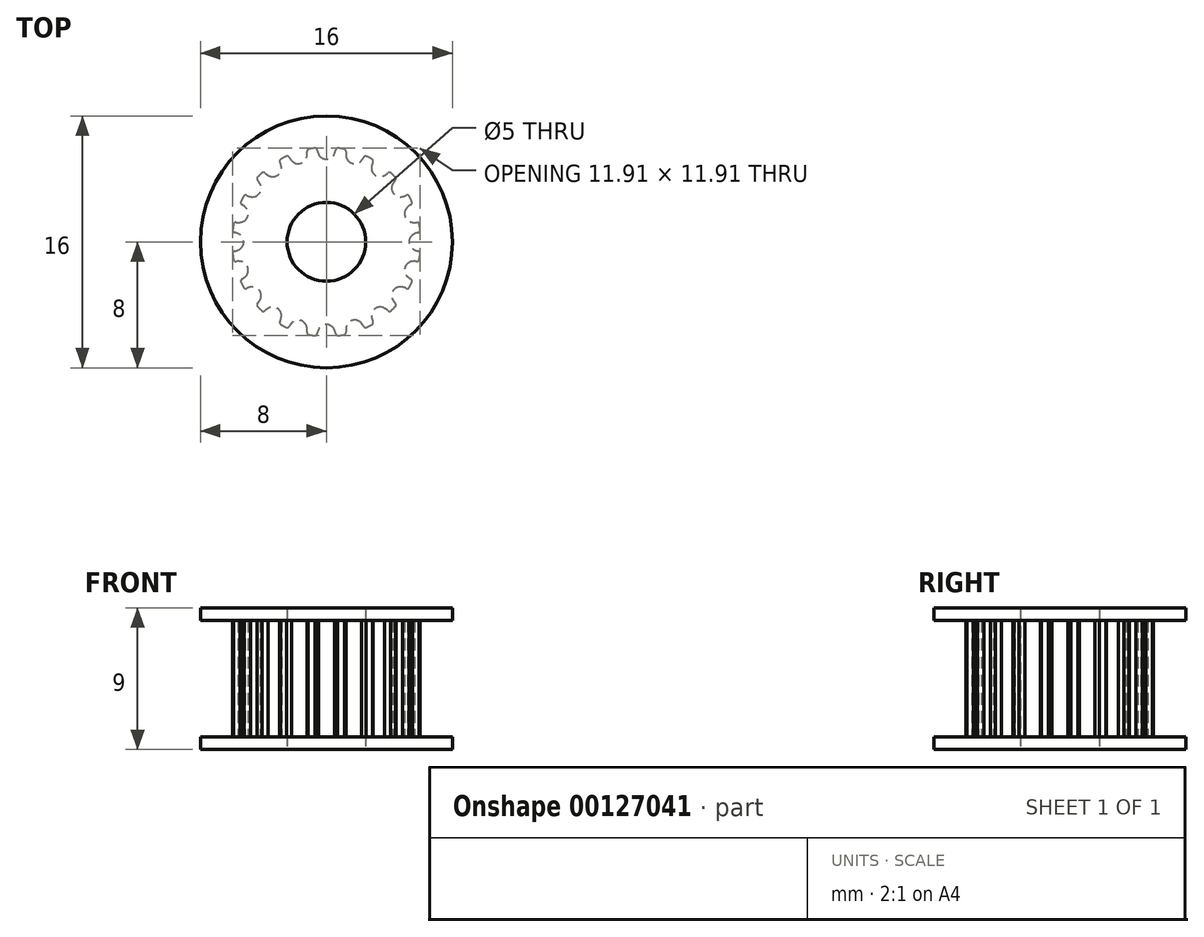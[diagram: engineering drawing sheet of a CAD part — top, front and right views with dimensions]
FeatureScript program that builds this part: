
annotation { "Feature Type Name" : "Feature", "Feature Type Description" : "" }
export const myFeature = defineFeature(function(context is Context, id is Id, definition is map)
    precondition{}
    {
        {
            var Q0;
            Q0=qCreatedBy(makeId("Top.planeOp"),FACE);
            var sketch = newSketch(context, id + "F0", { "sketchPlane" : qUnion([Q0])});
            skLineSegment(sketch, "E0", {"start": v(-19.17, 17.78) * mm, "end": v(-18.17, 17.78) * mm});
            skLineSegment(sketch, "E1", {"start": v(-18.17, 17.78) * mm, "end": v(-18.17, 18.4) * mm});
            skArc(sketch, "E2", {"start": v(-18.67, 18.85) * mm, "mid": v(-18.88, 19.07) * mm, "end": v(-19.17, 19.16) * mm});
            skArc(sketch, "E3", {"start": v(-18.58, 18.54) * mm, "mid": v(-18.61, 18.7) * mm, "end": v(-18.67, 18.85) * mm});
            skArc(sketch, "E4", {"start": v(-18.58, 18.54) * mm, "mid": v(-18.53, 18.44) * mm, "end": v(-18.43, 18.4) * mm});
            skLineSegment(sketch, "E5", {"start": v(-18.43, 18.4) * mm, "end": v(-18.17, 18.4) * mm});
            skArc(sketch, "E6.0.MirrorCS", {"start": v(-19.67, 18.85) * mm, "mid": v(-19.47, 19.07) * mm, "end": v(-19.17, 19.16) * mm});
            skArc(sketch, "E7.0.MirrorCS", {"start": v(-19.76, 18.54) * mm, "mid": v(-19.73, 18.7) * mm, "end": v(-19.67, 18.85) * mm});
            skArc(sketch, "E8.0.MirrorCS", {"start": v(-19.76, 18.54) * mm, "mid": v(-19.81, 18.44) * mm, "end": v(-19.91, 18.4) * mm});
            skLineSegment(sketch, "E9.0.MirrorCS", {"start": v(-19.91, 18.4) * mm, "end": v(-20.17, 18.4) * mm});
            skLineSegment(sketch, "E10.0.MirrorCS", {"start": v(-20.17, 17.78) * mm, "end": v(-20.17, 18.4) * mm});
            skLineSegment(sketch, "E11.0.MirrorCS", {"start": v(-19.17, 17.78) * mm, "end": v(-20.17, 17.78) * mm});
            skLineSegment(sketch, "E12.direction1", {"start": v(-20.17, 17.78) * mm, "end": v(-18.17, 17.78) * mm, "construction": true});
            skLineSegment(sketch, "E13", {"start": v(-20.17, 18.15) * mm, "end": v(-18.17, 18.15) * mm, "construction": true});
            skPoint(sketch, "E14", {"position": v(0, -5.25) * mm});
            skArc(sketch, "E15", {"start": v(0.51, -5.6) * mm, "mid": v(0, -5.25) * mm, "end": v(-0.51, -5.6) * mm});
            skArc(sketch, "E16", {"start": v(-0.51, -5.6) * mm, "mid": v(-0.56, -5.71) * mm, "end": v(-0.59, -5.83) * mm});
            skArc(sketch, "E17", {"start": v(0.59, -5.83) * mm, "mid": v(0.56, -5.71) * mm, "end": v(0.51, -5.6) * mm});
            skArc(sketch, "E18", {"start": v(0.72, -5.96) * mm, "mid": v(0.94, -5.93) * mm, "end": v(1.16, -5.89) * mm});
            skArc(sketch, "E19", {"start": v(0.59, -5.83) * mm, "mid": v(0.66, -5.94) * mm, "end": v(0.8, -5.95) * mm});
            skArc(sketch, "E20", {"start": v(-0.59, -5.83) * mm, "mid": v(-0.66, -5.94) * mm, "end": v(-0.8, -5.95) * mm});
            skArc(sketch, "E21.1.0", {"start": v(2.22, -5.16) * mm, "mid": v(1.62, -5) * mm, "end": v(1.24, -5.48) * mm});
            skPoint(sketch, "E21.1.1", {"position": v(1.62, -5) * mm});
            skArc(sketch, "E21.1.2", {"start": v(1.24, -5.48) * mm, "mid": v(1.23, -5.6) * mm, "end": v(1.24, -5.73) * mm});
            skArc(sketch, "E21.1.3", {"start": v(2.36, -5.37) * mm, "mid": v(2.47, -5.44) * mm, "end": v(2.6, -5.41) * mm});
            skArc(sketch, "E21.1.4", {"start": v(1.24, -5.73) * mm, "mid": v(1.2, -5.85) * mm, "end": v(1.08, -5.9) * mm});
            skArc(sketch, "E21.1.5", {"start": v(2.36, -5.37) * mm, "mid": v(2.3, -5.26) * mm, "end": v(2.22, -5.16) * mm});
            skArc(sketch, "E22.3.2.0", {"start": v(3.7, -4.22) * mm, "mid": v(3.09, -4.25) * mm, "end": v(2.87, -4.83) * mm});
            skPoint(sketch, "E22.4.2.0", {"position": v(3.09, -4.25) * mm});
            skArc(sketch, "E22.5.2.0", {"start": v(2.87, -4.83) * mm, "mid": v(2.9, -4.95) * mm, "end": v(2.95, -5.07) * mm});
            skArc(sketch, "E22.9.2.0", {"start": v(3.9, -4.37) * mm, "mid": v(4.03, -4.41) * mm, "end": v(4.14, -4.35) * mm});
            skArc(sketch, "E22.13.2.0", {"start": v(2.95, -5.07) * mm, "mid": v(2.95, -5.2) * mm, "end": v(2.85, -5.28) * mm});
            skArc(sketch, "E22.17.2.0", {"start": v(3.9, -4.37) * mm, "mid": v(3.81, -4.3) * mm, "end": v(3.7, -4.22) * mm});
            skArc(sketch, "E22.3.3.0", {"start": v(4.83, -2.87) * mm, "mid": v(4.25, -3.09) * mm, "end": v(4.22, -3.7) * mm});
            skPoint(sketch, "E22.4.3.0", {"position": v(4.25, -3.09) * mm});
            skArc(sketch, "E22.5.3.0", {"start": v(4.22, -3.7) * mm, "mid": v(4.3, -3.81) * mm, "end": v(4.37, -3.9) * mm});
            skArc(sketch, "E22.9.3.0", {"start": v(5.07, -2.95) * mm, "mid": v(5.2, -2.95) * mm, "end": v(5.28, -2.85) * mm});
            skArc(sketch, "E22.13.3.0", {"start": v(4.37, -3.9) * mm, "mid": v(4.41, -4.03) * mm, "end": v(4.35, -4.14) * mm});
            skArc(sketch, "E22.17.3.0", {"start": v(5.07, -2.95) * mm, "mid": v(4.95, -2.9) * mm, "end": v(4.83, -2.87) * mm});
            skArc(sketch, "E22.3.4.0", {"start": v(5.48, -1.24) * mm, "mid": v(5, -1.62) * mm, "end": v(5.16, -2.22) * mm});
            skPoint(sketch, "E22.4.4.0", {"position": v(5, -1.62) * mm});
            skArc(sketch, "E22.5.4.0", {"start": v(5.16, -2.22) * mm, "mid": v(5.26, -2.3) * mm, "end": v(5.37, -2.36) * mm});
            skArc(sketch, "E22.9.4.0", {"start": v(5.73, -1.24) * mm, "mid": v(5.85, -1.2) * mm, "end": v(5.9, -1.08) * mm});
            skArc(sketch, "E22.13.4.0", {"start": v(5.37, -2.36) * mm, "mid": v(5.44, -2.47) * mm, "end": v(5.41, -2.6) * mm});
            skArc(sketch, "E22.17.4.0", {"start": v(5.73, -1.24) * mm, "mid": v(5.6, -1.23) * mm, "end": v(5.48, -1.24) * mm});
            skArc(sketch, "E22.3.5.0", {"start": v(5.6, 0.51) * mm, "mid": v(5.25, 0) * mm, "end": v(5.6, -0.51) * mm});
            skPoint(sketch, "E22.4.5.0", {"position": v(5.25, 0) * mm});
            skArc(sketch, "E22.5.5.0", {"start": v(5.6, -0.51) * mm, "mid": v(5.71, -0.56) * mm, "end": v(5.83, -0.59) * mm});
            skArc(sketch, "E22.9.5.0", {"start": v(5.83, 0.59) * mm, "mid": v(5.94, 0.66) * mm, "end": v(5.95, 0.8) * mm});
            skArc(sketch, "E22.13.5.0", {"start": v(5.83, -0.59) * mm, "mid": v(5.94, -0.66) * mm, "end": v(5.95, -0.8) * mm});
            skArc(sketch, "E22.17.5.0", {"start": v(5.83, 0.59) * mm, "mid": v(5.71, 0.56) * mm, "end": v(5.6, 0.51) * mm});
            skArc(sketch, "E22.3.6.0", {"start": v(5.16, 2.22) * mm, "mid": v(5, 1.62) * mm, "end": v(5.48, 1.24) * mm});
            skPoint(sketch, "E22.4.6.0", {"position": v(5, 1.62) * mm});
            skArc(sketch, "E22.5.6.0", {"start": v(5.48, 1.24) * mm, "mid": v(5.6, 1.23) * mm, "end": v(5.73, 1.24) * mm});
            skArc(sketch, "E22.9.6.0", {"start": v(5.37, 2.36) * mm, "mid": v(5.44, 2.47) * mm, "end": v(5.41, 2.6) * mm});
            skArc(sketch, "E22.13.6.0", {"start": v(5.73, 1.24) * mm, "mid": v(5.85, 1.2) * mm, "end": v(5.9, 1.08) * mm});
            skArc(sketch, "E22.17.6.0", {"start": v(5.37, 2.36) * mm, "mid": v(5.26, 2.3) * mm, "end": v(5.16, 2.22) * mm});
            skArc(sketch, "E22.3.7.0", {"start": v(4.22, 3.7) * mm, "mid": v(4.25, 3.09) * mm, "end": v(4.83, 2.87) * mm});
            skPoint(sketch, "E22.4.7.0", {"position": v(4.25, 3.09) * mm});
            skArc(sketch, "E22.5.7.0", {"start": v(4.83, 2.87) * mm, "mid": v(4.95, 2.9) * mm, "end": v(5.07, 2.95) * mm});
            skArc(sketch, "E22.9.7.0", {"start": v(4.37, 3.9) * mm, "mid": v(4.41, 4.03) * mm, "end": v(4.35, 4.14) * mm});
            skArc(sketch, "E22.13.7.0", {"start": v(5.07, 2.95) * mm, "mid": v(5.2, 2.95) * mm, "end": v(5.28, 2.85) * mm});
            skArc(sketch, "E22.17.7.0", {"start": v(4.37, 3.9) * mm, "mid": v(4.3, 3.81) * mm, "end": v(4.22, 3.7) * mm});
            skArc(sketch, "E22.3.8.0", {"start": v(2.87, 4.83) * mm, "mid": v(3.09, 4.25) * mm, "end": v(3.7, 4.22) * mm});
            skPoint(sketch, "E22.4.8.0", {"position": v(3.09, 4.25) * mm});
            skArc(sketch, "E22.5.8.0", {"start": v(3.7, 4.22) * mm, "mid": v(3.81, 4.3) * mm, "end": v(3.9, 4.37) * mm});
            skArc(sketch, "E22.9.8.0", {"start": v(2.95, 5.07) * mm, "mid": v(2.95, 5.2) * mm, "end": v(2.85, 5.28) * mm});
            skArc(sketch, "E22.13.8.0", {"start": v(3.9, 4.37) * mm, "mid": v(4.03, 4.41) * mm, "end": v(4.14, 4.35) * mm});
            skArc(sketch, "E22.17.8.0", {"start": v(2.95, 5.07) * mm, "mid": v(2.9, 4.95) * mm, "end": v(2.87, 4.83) * mm});
            skArc(sketch, "E22.3.9.0", {"start": v(1.24, 5.48) * mm, "mid": v(1.62, 5) * mm, "end": v(2.22, 5.16) * mm});
            skPoint(sketch, "E22.4.9.0", {"position": v(1.62, 5) * mm});
            skArc(sketch, "E22.5.9.0", {"start": v(2.22, 5.16) * mm, "mid": v(2.3, 5.26) * mm, "end": v(2.36, 5.37) * mm});
            skArc(sketch, "E22.9.9.0", {"start": v(1.24, 5.73) * mm, "mid": v(1.2, 5.85) * mm, "end": v(1.08, 5.9) * mm});
            skArc(sketch, "E22.13.9.0", {"start": v(2.36, 5.37) * mm, "mid": v(2.47, 5.44) * mm, "end": v(2.6, 5.41) * mm});
            skArc(sketch, "E22.17.9.0", {"start": v(1.24, 5.73) * mm, "mid": v(1.23, 5.6) * mm, "end": v(1.24, 5.48) * mm});
            skArc(sketch, "E22.3.10.0", {"start": v(-0.51, 5.6) * mm, "mid": v(0, 5.25) * mm, "end": v(0.51, 5.6) * mm});
            skPoint(sketch, "E22.4.10.0", {"position": v(0, 5.25) * mm});
            skArc(sketch, "E22.5.10.0", {"start": v(0.51, 5.6) * mm, "mid": v(0.56, 5.71) * mm, "end": v(0.59, 5.83) * mm});
            skArc(sketch, "E22.9.10.0", {"start": v(-0.59, 5.83) * mm, "mid": v(-0.66, 5.94) * mm, "end": v(-0.8, 5.95) * mm});
            skArc(sketch, "E22.13.10.0", {"start": v(0.59, 5.83) * mm, "mid": v(0.66, 5.94) * mm, "end": v(0.8, 5.95) * mm});
            skArc(sketch, "E22.17.10.0", {"start": v(-0.59, 5.83) * mm, "mid": v(-0.56, 5.71) * mm, "end": v(-0.51, 5.6) * mm});
            skArc(sketch, "E22.3.11.0", {"start": v(-2.22, 5.16) * mm, "mid": v(-1.62, 5) * mm, "end": v(-1.24, 5.48) * mm});
            skPoint(sketch, "E22.4.11.0", {"position": v(-1.62, 5) * mm});
            skArc(sketch, "E22.5.11.0", {"start": v(-1.24, 5.48) * mm, "mid": v(-1.23, 5.6) * mm, "end": v(-1.24, 5.73) * mm});
            skArc(sketch, "E22.9.11.0", {"start": v(-2.36, 5.37) * mm, "mid": v(-2.47, 5.44) * mm, "end": v(-2.6, 5.41) * mm});
            skArc(sketch, "E22.13.11.0", {"start": v(-1.24, 5.73) * mm, "mid": v(-1.2, 5.85) * mm, "end": v(-1.08, 5.9) * mm});
            skArc(sketch, "E22.17.11.0", {"start": v(-2.36, 5.37) * mm, "mid": v(-2.3, 5.26) * mm, "end": v(-2.22, 5.16) * mm});
            skArc(sketch, "E22.3.12.0", {"start": v(-3.7, 4.22) * mm, "mid": v(-3.09, 4.25) * mm, "end": v(-2.87, 4.83) * mm});
            skPoint(sketch, "E22.4.12.0", {"position": v(-3.09, 4.25) * mm});
            skArc(sketch, "E22.5.12.0", {"start": v(-2.87, 4.83) * mm, "mid": v(-2.9, 4.95) * mm, "end": v(-2.95, 5.07) * mm});
            skArc(sketch, "E22.9.12.0", {"start": v(-3.9, 4.37) * mm, "mid": v(-4.03, 4.41) * mm, "end": v(-4.14, 4.35) * mm});
            skArc(sketch, "E22.13.12.0", {"start": v(-2.95, 5.07) * mm, "mid": v(-2.95, 5.2) * mm, "end": v(-2.85, 5.28) * mm});
            skArc(sketch, "E22.17.12.0", {"start": v(-3.9, 4.37) * mm, "mid": v(-3.81, 4.3) * mm, "end": v(-3.7, 4.22) * mm});
            skArc(sketch, "E22.3.13.0", {"start": v(-4.83, 2.87) * mm, "mid": v(-4.25, 3.09) * mm, "end": v(-4.22, 3.7) * mm});
            skPoint(sketch, "E22.4.13.0", {"position": v(-4.25, 3.09) * mm});
            skArc(sketch, "E22.5.13.0", {"start": v(-4.22, 3.7) * mm, "mid": v(-4.3, 3.81) * mm, "end": v(-4.37, 3.9) * mm});
            skArc(sketch, "E22.9.13.0", {"start": v(-5.07, 2.95) * mm, "mid": v(-5.2, 2.95) * mm, "end": v(-5.28, 2.85) * mm});
            skArc(sketch, "E22.13.13.0", {"start": v(-4.37, 3.9) * mm, "mid": v(-4.41, 4.03) * mm, "end": v(-4.35, 4.14) * mm});
            skArc(sketch, "E22.17.13.0", {"start": v(-5.07, 2.95) * mm, "mid": v(-4.95, 2.9) * mm, "end": v(-4.83, 2.87) * mm});
            skArc(sketch, "E22.3.14.0", {"start": v(-5.48, 1.24) * mm, "mid": v(-5, 1.62) * mm, "end": v(-5.16, 2.22) * mm});
            skPoint(sketch, "E22.4.14.0", {"position": v(-5, 1.62) * mm});
            skArc(sketch, "E22.5.14.0", {"start": v(-5.16, 2.22) * mm, "mid": v(-5.26, 2.3) * mm, "end": v(-5.37, 2.36) * mm});
            skArc(sketch, "E22.9.14.0", {"start": v(-5.73, 1.24) * mm, "mid": v(-5.85, 1.2) * mm, "end": v(-5.9, 1.08) * mm});
            skArc(sketch, "E22.13.14.0", {"start": v(-5.37, 2.36) * mm, "mid": v(-5.44, 2.47) * mm, "end": v(-5.41, 2.6) * mm});
            skArc(sketch, "E22.17.14.0", {"start": v(-5.73, 1.24) * mm, "mid": v(-5.6, 1.23) * mm, "end": v(-5.48, 1.24) * mm});
            skArc(sketch, "E22.3.15.0", {"start": v(-5.6, -0.51) * mm, "mid": v(-5.25, 0) * mm, "end": v(-5.6, 0.51) * mm});
            skPoint(sketch, "E22.4.15.0", {"position": v(-5.25, 0) * mm});
            skArc(sketch, "E22.5.15.0", {"start": v(-5.6, 0.51) * mm, "mid": v(-5.71, 0.56) * mm, "end": v(-5.83, 0.59) * mm});
            skArc(sketch, "E22.9.15.0", {"start": v(-5.83, -0.59) * mm, "mid": v(-5.94, -0.66) * mm, "end": v(-5.95, -0.8) * mm});
            skArc(sketch, "E22.13.15.0", {"start": v(-5.83, 0.59) * mm, "mid": v(-5.94, 0.66) * mm, "end": v(-5.95, 0.8) * mm});
            skArc(sketch, "E22.17.15.0", {"start": v(-5.83, -0.59) * mm, "mid": v(-5.71, -0.56) * mm, "end": v(-5.6, -0.51) * mm});
            skArc(sketch, "E22.3.16.0", {"start": v(-5.16, -2.22) * mm, "mid": v(-5, -1.62) * mm, "end": v(-5.48, -1.24) * mm});
            skPoint(sketch, "E22.4.16.0", {"position": v(-5, -1.62) * mm});
            skArc(sketch, "E22.5.16.0", {"start": v(-5.48, -1.24) * mm, "mid": v(-5.6, -1.23) * mm, "end": v(-5.73, -1.24) * mm});
            skArc(sketch, "E22.9.16.0", {"start": v(-5.37, -2.36) * mm, "mid": v(-5.44, -2.47) * mm, "end": v(-5.41, -2.6) * mm});
            skArc(sketch, "E22.13.16.0", {"start": v(-5.73, -1.24) * mm, "mid": v(-5.85, -1.2) * mm, "end": v(-5.9, -1.08) * mm});
            skArc(sketch, "E22.17.16.0", {"start": v(-5.37, -2.36) * mm, "mid": v(-5.26, -2.3) * mm, "end": v(-5.16, -2.22) * mm});
            skArc(sketch, "E22.3.17.0", {"start": v(-4.22, -3.7) * mm, "mid": v(-4.25, -3.09) * mm, "end": v(-4.83, -2.87) * mm});
            skPoint(sketch, "E22.4.17.0", {"position": v(-4.25, -3.09) * mm});
            skArc(sketch, "E22.5.17.0", {"start": v(-4.83, -2.87) * mm, "mid": v(-4.95, -2.9) * mm, "end": v(-5.07, -2.95) * mm});
            skArc(sketch, "E22.9.17.0", {"start": v(-4.37, -3.9) * mm, "mid": v(-4.41, -4.03) * mm, "end": v(-4.35, -4.14) * mm});
            skArc(sketch, "E22.13.17.0", {"start": v(-5.07, -2.95) * mm, "mid": v(-5.2, -2.95) * mm, "end": v(-5.28, -2.85) * mm});
            skArc(sketch, "E22.17.17.0", {"start": v(-4.37, -3.9) * mm, "mid": v(-4.3, -3.81) * mm, "end": v(-4.22, -3.7) * mm});
            skArc(sketch, "E22.3.18.0", {"start": v(-2.87, -4.83) * mm, "mid": v(-3.09, -4.25) * mm, "end": v(-3.7, -4.22) * mm});
            skPoint(sketch, "E22.4.18.0", {"position": v(-3.09, -4.25) * mm});
            skArc(sketch, "E22.5.18.0", {"start": v(-3.7, -4.22) * mm, "mid": v(-3.81, -4.3) * mm, "end": v(-3.9, -4.37) * mm});
            skArc(sketch, "E22.9.18.0", {"start": v(-2.95, -5.07) * mm, "mid": v(-2.95, -5.2) * mm, "end": v(-2.85, -5.28) * mm});
            skArc(sketch, "E22.13.18.0", {"start": v(-3.9, -4.37) * mm, "mid": v(-4.03, -4.41) * mm, "end": v(-4.14, -4.35) * mm});
            skArc(sketch, "E22.17.18.0", {"start": v(-2.95, -5.07) * mm, "mid": v(-2.9, -4.95) * mm, "end": v(-2.87, -4.83) * mm});
            skArc(sketch, "E22.3.19.0", {"start": v(-1.24, -5.48) * mm, "mid": v(-1.62, -5) * mm, "end": v(-2.22, -5.16) * mm});
            skPoint(sketch, "E22.4.19.0", {"position": v(-1.62, -5) * mm});
            skArc(sketch, "E22.5.19.0", {"start": v(-2.22, -5.16) * mm, "mid": v(-2.3, -5.26) * mm, "end": v(-2.36, -5.37) * mm});
            skArc(sketch, "E22.9.19.0", {"start": v(-1.24, -5.73) * mm, "mid": v(-1.2, -5.85) * mm, "end": v(-1.08, -5.9) * mm});
            skArc(sketch, "E22.13.19.0", {"start": v(-2.36, -5.37) * mm, "mid": v(-2.47, -5.44) * mm, "end": v(-2.6, -5.41) * mm});
            skArc(sketch, "E22.17.19.0", {"start": v(-1.24, -5.73) * mm, "mid": v(-1.23, -5.6) * mm, "end": v(-1.24, -5.48) * mm});
            skArc(sketch, "E23.trimOffspring", {"start": v(2.52, -5.44) * mm, "mid": v(2.72, -5.35) * mm, "end": v(2.92, -5.24) * mm});
            skArc(sketch, "E24.trimOffspring", {"start": v(4.08, -4.4) * mm, "mid": v(4.24, -4.24) * mm, "end": v(4.4, -4.08) * mm});
            skArc(sketch, "E25.trimOffspring", {"start": v(5.24, -2.92) * mm, "mid": v(5.33, -2.76) * mm, "end": v(5.41, -2.6) * mm});
            skArc(sketch, "E26.trimOffspring", {"start": v(5.89, -1.16) * mm, "mid": v(5.93, -0.94) * mm, "end": v(5.96, -0.72) * mm});
            skArc(sketch, "E27.trimOffspring", {"start": v(5.44, 2.52) * mm, "mid": v(5.35, 2.72) * mm, "end": v(5.24, 2.92) * mm});
            skArc(sketch, "E28.trimOffspring", {"start": v(4.4, 4.08) * mm, "mid": v(4.24, 4.24) * mm, "end": v(4.08, 4.4) * mm});
            skArc(sketch, "E29.trimOffspring", {"start": v(5.96, 0.72) * mm, "mid": v(5.93, 0.94) * mm, "end": v(5.89, 1.16) * mm});
            skArc(sketch, "E30.trimOffspring", {"start": v(2.92, 5.24) * mm, "mid": v(2.72, 5.35) * mm, "end": v(2.52, 5.44) * mm});
            skArc(sketch, "E31.trimOffspring", {"start": v(1.16, 5.89) * mm, "mid": v(0.94, 5.93) * mm, "end": v(0.72, 5.96) * mm});
            skArc(sketch, "E32.trimOffspring", {"start": v(-0.72, 5.96) * mm, "mid": v(-0.94, 5.93) * mm, "end": v(-1.16, 5.89) * mm});
            skArc(sketch, "E33.trimOffspring", {"start": v(-2.52, 5.44) * mm, "mid": v(-2.72, 5.35) * mm, "end": v(-2.92, 5.24) * mm});
            skArc(sketch, "E34.trimOffspring", {"start": v(-4.08, 4.4) * mm, "mid": v(-4.24, 4.24) * mm, "end": v(-4.4, 4.08) * mm});
            skArc(sketch, "E35.trimOffspring", {"start": v(-5.24, 2.92) * mm, "mid": v(-5.35, 2.72) * mm, "end": v(-5.44, 2.52) * mm});
            skArc(sketch, "E36.trimOffspring", {"start": v(-5.89, 1.16) * mm, "mid": v(-5.93, 0.94) * mm, "end": v(-5.96, 0.72) * mm});
            skArc(sketch, "E37.trimOffspring", {"start": v(-5.96, -0.72) * mm, "mid": v(-5.93, -0.94) * mm, "end": v(-5.89, -1.16) * mm});
            skArc(sketch, "E38.trimOffspring", {"start": v(-5.44, -2.52) * mm, "mid": v(-5.35, -2.72) * mm, "end": v(-5.24, -2.92) * mm});
            skArc(sketch, "E39.trimOffspring", {"start": v(-4.4, -4.08) * mm, "mid": v(-4.24, -4.24) * mm, "end": v(-4.08, -4.4) * mm});
            skArc(sketch, "E40.trimOffspring", {"start": v(-2.92, -5.24) * mm, "mid": v(-2.72, -5.35) * mm, "end": v(-2.52, -5.44) * mm});
            skArc(sketch, "E41.trimOffspring", {"start": v(-1.16, -5.89) * mm, "mid": v(-0.94, -5.93) * mm, "end": v(-0.72, -5.96) * mm});
            skSolve(sketch);
        }
        {
            var Q0;
            Q0=makeQuery(id+"F0.imprint","IMPRINT",FACE,{"disambiguationData":[TD([[makeQuery(id+"F0.imprint","IMPRINT",EDGE,{"derivedFrom":sQuery(id+"F0.wireOp",EDGE,"E15")}),-1.0]])]});
            extrude(context, id + "F1", {"entities" : qUnion([Q0]), "depth" : 7.4 * mm});
        }
        {
            var Q0;
            Q0=makeQuery(id+"F1.opExtrude","CAP_FACE",FACE,{"disambiguationData":[OSD([sQuery(id+"F0.wireOp",EDGE,"E15"),sQuery(id+"F0.wireOp",EDGE,"E16"),sQuery(id+"F0.wireOp",EDGE,"E17"),sQuery(id+"F0.wireOp",EDGE,"E18"),sQuery(id+"F0.wireOp",EDGE,"E19"),sQuery(id+"F0.wireOp",EDGE,"E20"),sQuery(id+"F0.wireOp",EDGE,"E21.1.0"),sQuery(id+"F0.wireOp",EDGE,"E21.1.2"),sQuery(id+"F0.wireOp",EDGE,"E21.1.3"),sQuery(id+"F0.wireOp",EDGE,"E21.1.4"),sQuery(id+"F0.wireOp",EDGE,"E21.1.5"),sQuery(id+"F0.wireOp",EDGE,"E22.3.2.0"),sQuery(id+"F0.wireOp",EDGE,"E22.5.2.0"),sQuery(id+"F0.wireOp",EDGE,"E22.9.2.0"),sQuery(id+"F0.wireOp",EDGE,"E22.13.2.0"),sQuery(id+"F0.wireOp",EDGE,"E22.17.2.0"),sQuery(id+"F0.wireOp",EDGE,"E22.3.3.0"),sQuery(id+"F0.wireOp",EDGE,"E22.5.3.0"),sQuery(id+"F0.wireOp",EDGE,"E22.9.3.0"),sQuery(id+"F0.wireOp",EDGE,"E22.13.3.0"),sQuery(id+"F0.wireOp",EDGE,"E22.17.3.0"),sQuery(id+"F0.wireOp",EDGE,"E22.3.4.0"),sQuery(id+"F0.wireOp",EDGE,"E22.5.4.0"),sQuery(id+"F0.wireOp",EDGE,"E22.9.4.0"),sQuery(id+"F0.wireOp",EDGE,"E22.13.4.0"),sQuery(id+"F0.wireOp",EDGE,"E22.17.4.0"),sQuery(id+"F0.wireOp",EDGE,"E22.3.5.0"),sQuery(id+"F0.wireOp",EDGE,"E22.5.5.0"),sQuery(id+"F0.wireOp",EDGE,"E22.9.5.0"),sQuery(id+"F0.wireOp",EDGE,"E22.13.5.0"),sQuery(id+"F0.wireOp",EDGE,"E22.17.5.0"),sQuery(id+"F0.wireOp",EDGE,"E22.3.6.0"),sQuery(id+"F0.wireOp",EDGE,"E22.5.6.0"),sQuery(id+"F0.wireOp",EDGE,"E22.9.6.0"),sQuery(id+"F0.wireOp",EDGE,"E22.13.6.0"),sQuery(id+"F0.wireOp",EDGE,"E22.17.6.0"),sQuery(id+"F0.wireOp",EDGE,"E22.3.7.0"),sQuery(id+"F0.wireOp",EDGE,"E22.5.7.0"),sQuery(id+"F0.wireOp",EDGE,"E22.9.7.0"),sQuery(id+"F0.wireOp",EDGE,"E22.13.7.0"),sQuery(id+"F0.wireOp",EDGE,"E22.17.7.0"),sQuery(id+"F0.wireOp",EDGE,"E22.3.8.0"),sQuery(id+"F0.wireOp",EDGE,"E22.5.8.0"),sQuery(id+"F0.wireOp",EDGE,"E22.9.8.0"),sQuery(id+"F0.wireOp",EDGE,"E22.13.8.0"),sQuery(id+"F0.wireOp",EDGE,"E22.17.8.0"),sQuery(id+"F0.wireOp",EDGE,"E22.3.9.0"),sQuery(id+"F0.wireOp",EDGE,"E22.5.9.0"),sQuery(id+"F0.wireOp",EDGE,"E22.9.9.0"),sQuery(id+"F0.wireOp",EDGE,"E22.13.9.0"),sQuery(id+"F0.wireOp",EDGE,"E22.17.9.0"),sQuery(id+"F0.wireOp",EDGE,"E22.3.10.0"),sQuery(id+"F0.wireOp",EDGE,"E22.5.10.0"),sQuery(id+"F0.wireOp",EDGE,"E22.9.10.0"),sQuery(id+"F0.wireOp",EDGE,"E22.13.10.0"),sQuery(id+"F0.wireOp",EDGE,"E22.17.10.0"),sQuery(id+"F0.wireOp",EDGE,"E22.3.11.0"),sQuery(id+"F0.wireOp",EDGE,"E22.5.11.0"),sQuery(id+"F0.wireOp",EDGE,"E22.9.11.0"),sQuery(id+"F0.wireOp",EDGE,"E22.13.11.0"),sQuery(id+"F0.wireOp",EDGE,"E22.17.11.0"),sQuery(id+"F0.wireOp",EDGE,"E22.3.12.0"),sQuery(id+"F0.wireOp",EDGE,"E22.5.12.0"),sQuery(id+"F0.wireOp",EDGE,"E22.9.12.0"),sQuery(id+"F0.wireOp",EDGE,"E22.13.12.0"),sQuery(id+"F0.wireOp",EDGE,"E22.17.12.0"),sQuery(id+"F0.wireOp",EDGE,"E22.3.13.0"),sQuery(id+"F0.wireOp",EDGE,"E22.5.13.0"),sQuery(id+"F0.wireOp",EDGE,"E22.9.13.0"),sQuery(id+"F0.wireOp",EDGE,"E22.13.13.0"),sQuery(id+"F0.wireOp",EDGE,"E22.17.13.0"),sQuery(id+"F0.wireOp",EDGE,"E22.3.14.0"),sQuery(id+"F0.wireOp",EDGE,"E22.5.14.0"),sQuery(id+"F0.wireOp",EDGE,"E22.9.14.0"),sQuery(id+"F0.wireOp",EDGE,"E22.13.14.0"),sQuery(id+"F0.wireOp",EDGE,"E22.17.14.0"),sQuery(id+"F0.wireOp",EDGE,"E22.3.15.0"),sQuery(id+"F0.wireOp",EDGE,"E22.5.15.0"),sQuery(id+"F0.wireOp",EDGE,"E22.9.15.0"),sQuery(id+"F0.wireOp",EDGE,"E22.13.15.0"),sQuery(id+"F0.wireOp",EDGE,"E22.17.15.0"),sQuery(id+"F0.wireOp",EDGE,"E22.3.16.0"),sQuery(id+"F0.wireOp",EDGE,"E22.5.16.0"),sQuery(id+"F0.wireOp",EDGE,"E22.9.16.0"),sQuery(id+"F0.wireOp",EDGE,"E22.13.16.0"),sQuery(id+"F0.wireOp",EDGE,"E22.17.16.0"),sQuery(id+"F0.wireOp",EDGE,"E22.3.17.0"),sQuery(id+"F0.wireOp",EDGE,"E22.5.17.0"),sQuery(id+"F0.wireOp",EDGE,"E22.9.17.0"),sQuery(id+"F0.wireOp",EDGE,"E22.13.17.0"),sQuery(id+"F0.wireOp",EDGE,"E22.17.17.0"),sQuery(id+"F0.wireOp",EDGE,"E22.3.18.0"),sQuery(id+"F0.wireOp",EDGE,"E22.5.18.0"),sQuery(id+"F0.wireOp",EDGE,"E22.9.18.0"),sQuery(id+"F0.wireOp",EDGE,"E22.13.18.0"),sQuery(id+"F0.wireOp",EDGE,"E22.17.18.0"),sQuery(id+"F0.wireOp",EDGE,"E22.3.19.0"),sQuery(id+"F0.wireOp",EDGE,"E22.5.19.0"),sQuery(id+"F0.wireOp",EDGE,"E22.9.19.0"),sQuery(id+"F0.wireOp",EDGE,"E22.13.19.0"),sQuery(id+"F0.wireOp",EDGE,"E22.17.19.0"),sQuery(id+"F0.wireOp",EDGE,"E23.trimOffspring"),sQuery(id+"F0.wireOp",EDGE,"E24.trimOffspring"),sQuery(id+"F0.wireOp",EDGE,"E25.trimOffspring"),sQuery(id+"F0.wireOp",EDGE,"E26.trimOffspring"),sQuery(id+"F0.wireOp",EDGE,"E27.trimOffspring"),sQuery(id+"F0.wireOp",EDGE,"E28.trimOffspring"),sQuery(id+"F0.wireOp",EDGE,"E29.trimOffspring"),sQuery(id+"F0.wireOp",EDGE,"E30.trimOffspring"),sQuery(id+"F0.wireOp",EDGE,"E31.trimOffspring"),sQuery(id+"F0.wireOp",EDGE,"E32.trimOffspring"),sQuery(id+"F0.wireOp",EDGE,"E33.trimOffspring"),sQuery(id+"F0.wireOp",EDGE,"E34.trimOffspring"),sQuery(id+"F0.wireOp",EDGE,"E35.trimOffspring"),sQuery(id+"F0.wireOp",EDGE,"E36.trimOffspring"),sQuery(id+"F0.wireOp",EDGE,"E37.trimOffspring"),sQuery(id+"F0.wireOp",EDGE,"E38.trimOffspring"),sQuery(id+"F0.wireOp",EDGE,"E39.trimOffspring"),sQuery(id+"F0.wireOp",EDGE,"E40.trimOffspring"),sQuery(id+"F0.wireOp",EDGE,"E41.trimOffspring")])],"isStart":false});
            var sketch = newSketch(context, id + "F2", { "sketchPlane" : qUnion([Q0])});
            skCircle(sketch, "E42", {"center": v(0, 0) * mm, "radius": 8 * mm});
            skSolve(sketch);
        }
        {
            var Q0;
            Q0=qSketchRegion(id+"F2",true);
            extrude(context, id + "F3", {"entities" : qUnion([Q0]), "operationType" : NewBodyOperationType.ADD, "depth" : 0.8 * mm});
        }
        {
            var Q0;
            Q0=makeQuery(id+"F1.opExtrude","CAP_FACE",FACE,{"disambiguationData":[OSD([sQuery(id+"F0.wireOp",EDGE,"E15"),sQuery(id+"F0.wireOp",EDGE,"E16"),sQuery(id+"F0.wireOp",EDGE,"E17"),sQuery(id+"F0.wireOp",EDGE,"E18"),sQuery(id+"F0.wireOp",EDGE,"E19"),sQuery(id+"F0.wireOp",EDGE,"E20"),sQuery(id+"F0.wireOp",EDGE,"E21.1.0"),sQuery(id+"F0.wireOp",EDGE,"E21.1.2"),sQuery(id+"F0.wireOp",EDGE,"E21.1.3"),sQuery(id+"F0.wireOp",EDGE,"E21.1.4"),sQuery(id+"F0.wireOp",EDGE,"E21.1.5"),sQuery(id+"F0.wireOp",EDGE,"E22.3.2.0"),sQuery(id+"F0.wireOp",EDGE,"E22.5.2.0"),sQuery(id+"F0.wireOp",EDGE,"E22.9.2.0"),sQuery(id+"F0.wireOp",EDGE,"E22.13.2.0"),sQuery(id+"F0.wireOp",EDGE,"E22.17.2.0"),sQuery(id+"F0.wireOp",EDGE,"E22.3.3.0"),sQuery(id+"F0.wireOp",EDGE,"E22.5.3.0"),sQuery(id+"F0.wireOp",EDGE,"E22.9.3.0"),sQuery(id+"F0.wireOp",EDGE,"E22.13.3.0"),sQuery(id+"F0.wireOp",EDGE,"E22.17.3.0"),sQuery(id+"F0.wireOp",EDGE,"E22.3.4.0"),sQuery(id+"F0.wireOp",EDGE,"E22.5.4.0"),sQuery(id+"F0.wireOp",EDGE,"E22.9.4.0"),sQuery(id+"F0.wireOp",EDGE,"E22.13.4.0"),sQuery(id+"F0.wireOp",EDGE,"E22.17.4.0"),sQuery(id+"F0.wireOp",EDGE,"E22.3.5.0"),sQuery(id+"F0.wireOp",EDGE,"E22.5.5.0"),sQuery(id+"F0.wireOp",EDGE,"E22.9.5.0"),sQuery(id+"F0.wireOp",EDGE,"E22.13.5.0"),sQuery(id+"F0.wireOp",EDGE,"E22.17.5.0"),sQuery(id+"F0.wireOp",EDGE,"E22.3.6.0"),sQuery(id+"F0.wireOp",EDGE,"E22.5.6.0"),sQuery(id+"F0.wireOp",EDGE,"E22.9.6.0"),sQuery(id+"F0.wireOp",EDGE,"E22.13.6.0"),sQuery(id+"F0.wireOp",EDGE,"E22.17.6.0"),sQuery(id+"F0.wireOp",EDGE,"E22.3.7.0"),sQuery(id+"F0.wireOp",EDGE,"E22.5.7.0"),sQuery(id+"F0.wireOp",EDGE,"E22.9.7.0"),sQuery(id+"F0.wireOp",EDGE,"E22.13.7.0"),sQuery(id+"F0.wireOp",EDGE,"E22.17.7.0"),sQuery(id+"F0.wireOp",EDGE,"E22.3.8.0"),sQuery(id+"F0.wireOp",EDGE,"E22.5.8.0"),sQuery(id+"F0.wireOp",EDGE,"E22.9.8.0"),sQuery(id+"F0.wireOp",EDGE,"E22.13.8.0"),sQuery(id+"F0.wireOp",EDGE,"E22.17.8.0"),sQuery(id+"F0.wireOp",EDGE,"E22.3.9.0"),sQuery(id+"F0.wireOp",EDGE,"E22.5.9.0"),sQuery(id+"F0.wireOp",EDGE,"E22.9.9.0"),sQuery(id+"F0.wireOp",EDGE,"E22.13.9.0"),sQuery(id+"F0.wireOp",EDGE,"E22.17.9.0"),sQuery(id+"F0.wireOp",EDGE,"E22.3.10.0"),sQuery(id+"F0.wireOp",EDGE,"E22.5.10.0"),sQuery(id+"F0.wireOp",EDGE,"E22.9.10.0"),sQuery(id+"F0.wireOp",EDGE,"E22.13.10.0"),sQuery(id+"F0.wireOp",EDGE,"E22.17.10.0"),sQuery(id+"F0.wireOp",EDGE,"E22.3.11.0"),sQuery(id+"F0.wireOp",EDGE,"E22.5.11.0"),sQuery(id+"F0.wireOp",EDGE,"E22.9.11.0"),sQuery(id+"F0.wireOp",EDGE,"E22.13.11.0"),sQuery(id+"F0.wireOp",EDGE,"E22.17.11.0"),sQuery(id+"F0.wireOp",EDGE,"E22.3.12.0"),sQuery(id+"F0.wireOp",EDGE,"E22.5.12.0"),sQuery(id+"F0.wireOp",EDGE,"E22.9.12.0"),sQuery(id+"F0.wireOp",EDGE,"E22.13.12.0"),sQuery(id+"F0.wireOp",EDGE,"E22.17.12.0"),sQuery(id+"F0.wireOp",EDGE,"E22.3.13.0"),sQuery(id+"F0.wireOp",EDGE,"E22.5.13.0"),sQuery(id+"F0.wireOp",EDGE,"E22.9.13.0"),sQuery(id+"F0.wireOp",EDGE,"E22.13.13.0"),sQuery(id+"F0.wireOp",EDGE,"E22.17.13.0"),sQuery(id+"F0.wireOp",EDGE,"E22.3.14.0"),sQuery(id+"F0.wireOp",EDGE,"E22.5.14.0"),sQuery(id+"F0.wireOp",EDGE,"E22.9.14.0"),sQuery(id+"F0.wireOp",EDGE,"E22.13.14.0"),sQuery(id+"F0.wireOp",EDGE,"E22.17.14.0"),sQuery(id+"F0.wireOp",EDGE,"E22.3.15.0"),sQuery(id+"F0.wireOp",EDGE,"E22.5.15.0"),sQuery(id+"F0.wireOp",EDGE,"E22.9.15.0"),sQuery(id+"F0.wireOp",EDGE,"E22.13.15.0"),sQuery(id+"F0.wireOp",EDGE,"E22.17.15.0"),sQuery(id+"F0.wireOp",EDGE,"E22.3.16.0"),sQuery(id+"F0.wireOp",EDGE,"E22.5.16.0"),sQuery(id+"F0.wireOp",EDGE,"E22.9.16.0"),sQuery(id+"F0.wireOp",EDGE,"E22.13.16.0"),sQuery(id+"F0.wireOp",EDGE,"E22.17.16.0"),sQuery(id+"F0.wireOp",EDGE,"E22.3.17.0"),sQuery(id+"F0.wireOp",EDGE,"E22.5.17.0"),sQuery(id+"F0.wireOp",EDGE,"E22.9.17.0"),sQuery(id+"F0.wireOp",EDGE,"E22.13.17.0"),sQuery(id+"F0.wireOp",EDGE,"E22.17.17.0"),sQuery(id+"F0.wireOp",EDGE,"E22.3.18.0"),sQuery(id+"F0.wireOp",EDGE,"E22.5.18.0"),sQuery(id+"F0.wireOp",EDGE,"E22.9.18.0"),sQuery(id+"F0.wireOp",EDGE,"E22.13.18.0"),sQuery(id+"F0.wireOp",EDGE,"E22.17.18.0"),sQuery(id+"F0.wireOp",EDGE,"E22.3.19.0"),sQuery(id+"F0.wireOp",EDGE,"E22.5.19.0"),sQuery(id+"F0.wireOp",EDGE,"E22.9.19.0"),sQuery(id+"F0.wireOp",EDGE,"E22.13.19.0"),sQuery(id+"F0.wireOp",EDGE,"E22.17.19.0"),sQuery(id+"F0.wireOp",EDGE,"E23.trimOffspring"),sQuery(id+"F0.wireOp",EDGE,"E24.trimOffspring"),sQuery(id+"F0.wireOp",EDGE,"E25.trimOffspring"),sQuery(id+"F0.wireOp",EDGE,"E26.trimOffspring"),sQuery(id+"F0.wireOp",EDGE,"E27.trimOffspring"),sQuery(id+"F0.wireOp",EDGE,"E28.trimOffspring"),sQuery(id+"F0.wireOp",EDGE,"E29.trimOffspring"),sQuery(id+"F0.wireOp",EDGE,"E30.trimOffspring"),sQuery(id+"F0.wireOp",EDGE,"E31.trimOffspring"),sQuery(id+"F0.wireOp",EDGE,"E32.trimOffspring"),sQuery(id+"F0.wireOp",EDGE,"E33.trimOffspring"),sQuery(id+"F0.wireOp",EDGE,"E34.trimOffspring"),sQuery(id+"F0.wireOp",EDGE,"E35.trimOffspring"),sQuery(id+"F0.wireOp",EDGE,"E36.trimOffspring"),sQuery(id+"F0.wireOp",EDGE,"E37.trimOffspring"),sQuery(id+"F0.wireOp",EDGE,"E38.trimOffspring"),sQuery(id+"F0.wireOp",EDGE,"E39.trimOffspring"),sQuery(id+"F0.wireOp",EDGE,"E40.trimOffspring"),sQuery(id+"F0.wireOp",EDGE,"E41.trimOffspring")])],"isStart":true});
            var sketch = newSketch(context, id + "F4", { "sketchPlane" : qUnion([Q0])});
            skCircle(sketch, "E43", {"center": v(0, 0) * mm, "radius": 8 * mm});
            skSolve(sketch);
        }
        {
            var Q0;
            Q0=qSketchRegion(id+"F4",true);
            extrude(context, id + "F5", {"entities" : qUnion([Q0]), "operationType" : NewBodyOperationType.ADD, "depth" : 0.8 * mm});
        }
        {
            var Q0;
            Q0=makeQuery(id+"F5.opExtrude","CAP_FACE",FACE,{"disambiguationData":[OSD([sQuery(id+"F4.wireOp",EDGE,"E43")])],"isStart":false});
            var sketch = newSketch(context, id + "F6", { "sketchPlane" : qUnion([Q0])});
            skCircle(sketch, "E44", {"center": v(0, 0) * mm, "radius": 2.5 * mm});
            skSolve(sketch);
        }
        {
            var Q0;
            Q0=qSketchRegion(id+"F6",true);
            extrude(context, id + "F7", {"entities" : qUnion([Q0]), "operationType" : NewBodyOperationType.REMOVE, "endBound" : BoundingType.THROUGH_ALL, "oppositeDirection" : true, "depth" : 25 * mm});
        }
    });
